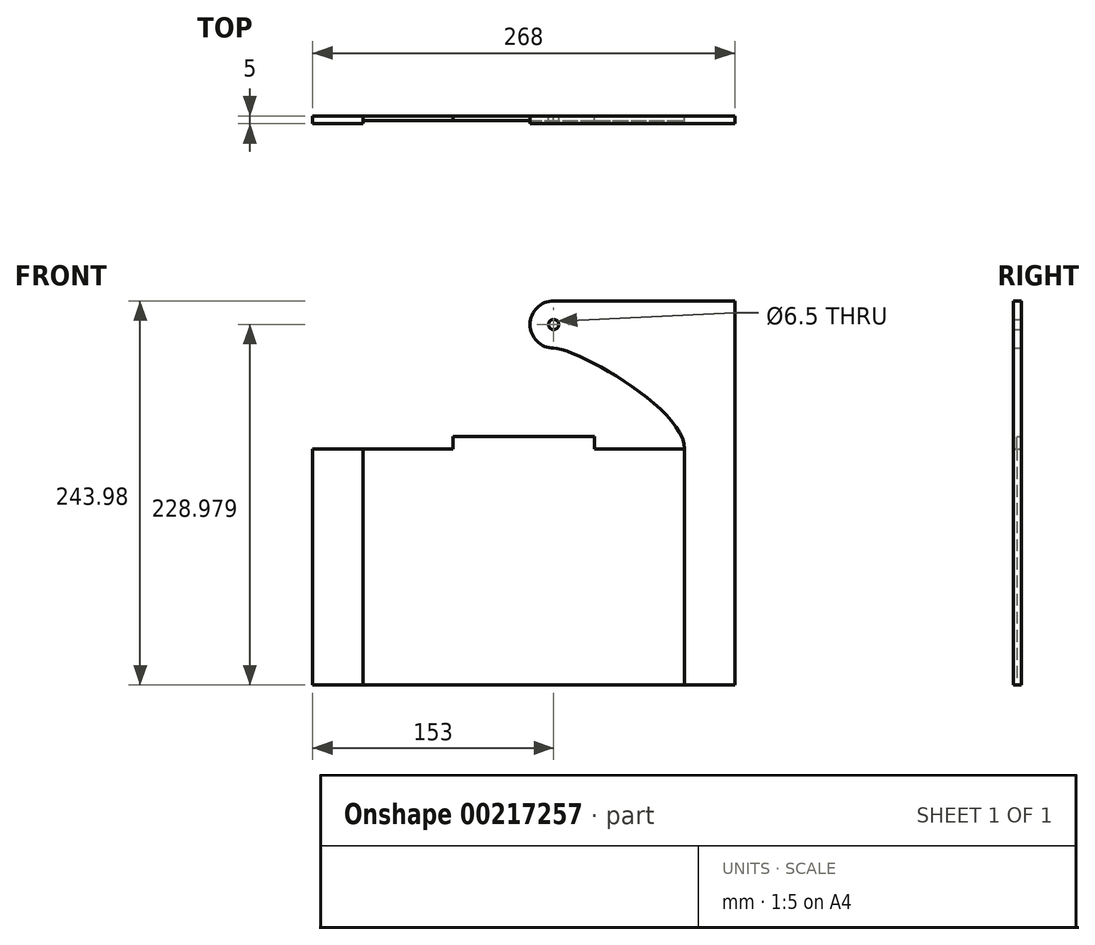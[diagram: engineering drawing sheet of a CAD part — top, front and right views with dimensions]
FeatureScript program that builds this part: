
annotation { "Feature Type Name" : "Feature", "Feature Type Description" : "" }
export const myFeature = defineFeature(function(context is Context, id is Id, definition is map)
    precondition{}
    {
        {
            var Q0;
            Q0=qCreatedBy(makeId("Front.planeOp"),FACE);
            var sketch = newSketch(context, id + "F0", { "sketchPlane" : qUnion([Q0])});
            skLineSegment(sketch, "E0.bottom", {"start": v(-134, 75) * mm, "end": v(134, 75) * mm});
            skLineSegment(sketch, "E0.top", {"start": v(-134, -75) * mm, "end": v(134, -75) * mm});
            skLineSegment(sketch, "E0.left", {"start": v(-134, 75) * mm, "end": v(-134, -75) * mm});
            skLineSegment(sketch, "E0.right", {"start": v(134, 75) * mm, "end": v(134, -75) * mm});
            skPoint(sketch, "E0.middle", {"position": v(0, 0) * mm});
            skPoint(sketch, "E1", {"position": v(-102, 75) * mm});
            skPoint(sketch, "E2", {"position": v(102, 75) * mm});
            skLineSegment(sketch, "E3", {"start": v(-102, 75) * mm, "end": v(-102, -75) * mm});
            skLineSegment(sketch, "E4", {"start": v(102, 75) * mm, "end": v(102, -75) * mm});
            skLineSegment(sketch, "E5.bottom", {"start": v(-134, 75) * mm, "end": v(-104, 75) * mm});
            skLineSegment(sketch, "E6.MirrorCS", {"start": v(102, 75) * mm, "end": v(104, 168.98) * mm});
            skLineSegment(sketch, "E7", {"start": v(134, 75) * mm, "end": v(134, 168.98) * mm});
            skLineSegment(sketch, "E8", {"start": v(134, 168.98) * mm, "end": v(104, 168.98) * mm});
            skPoint(sketch, "E9", {"position": v(0, 75) * mm});
            skLineSegment(sketch, "E10", {"start": v(0, 75) * mm, "end": v(45, 75) * mm});
            skLineSegment(sketch, "E11", {"start": v(0, 75) * mm, "end": v(-45, 75) * mm});
            skLineSegment(sketch, "E12.bottom", {"start": v(-45, 75) * mm, "end": v(45, 75) * mm});
            skLineSegment(sketch, "E12.top", {"start": v(-45, 83) * mm, "end": v(45, 83) * mm});
            skLineSegment(sketch, "E12.left", {"start": v(-45, 75) * mm, "end": v(-45, 83) * mm});
            skLineSegment(sketch, "E12.right", {"start": v(45, 75) * mm, "end": v(45, 83) * mm});
            skLineSegment(sketch, "E13", {"start": v(104, 168.98) * mm, "end": v(19, 168.98) * mm});
            skLineSegment(sketch, "E14", {"start": v(19, 168.98) * mm, "end": v(19, 138.98) * mm});
            skArc(sketch, "E15", {"start": v(19, 168.98) * mm, "mid": v(4, 153.98) * mm, "end": v(19, 138.98) * mm});
            skFitSpline(sketch, "E16", {"points": [v(19, 138.98) * mm, v(102, 75) * mm], "startDerivative": vector(45, -0.76) * mm, "endDerivative": vector(-1.6, -74.98) * mm});
            skLineSegment(sketch, "E17", {"start": v(0, 0) * mm, "end": v(0, -16.46) * mm});
            skArc(sketch, "E18.MirrorCS", {"start": v(-19, 168.98) * mm, "mid": v(-4, 153.98) * mm, "end": v(-19, 138.98) * mm});
            skFitSpline(sketch, "E19.MirrorCS", {"points": [v(-19, 138.98) * mm, v(-102, 75) * mm], "startDerivative": vector(-45, -0.76) * mm, "endDerivative": vector(1.6, -74.98) * mm});
            skLineSegment(sketch, "E20.MirrorCS", {"start": v(-104, 168.98) * mm, "end": v(-19, 168.98) * mm});
            skLineSegment(sketch, "E21.MirrorCS", {"start": v(-134, 168.98) * mm, "end": v(-104, 168.98) * mm});
            skLineSegment(sketch, "E22.MirrorCS", {"start": v(-134, 75) * mm, "end": v(-134, 168.98) * mm});
            skCircle(sketch, "E23", {"center": v(-19, 153.98) * mm, "radius": 3.25 * mm});
            skCircle(sketch, "E24.MirrorC", {"center": v(19, 153.98) * mm, "radius": 3.25 * mm});
            skSolve(sketch);
        }
        {
            var Q0;
            {var subQ0=sQuery(id+"F0.wireOp",EDGE,"E12.top");Q0=makeQuery(id+"F0.imprint","IMPRINT",FACE,{"disambiguationData":[TD([[makeQuery(id+"F0.imprint","IMPRINT",EDGE,{"derivedFrom":subQ0}),-1.0]])]});}
            var Q1;
            {var subQ0=sQuery(id+"F0.wireOp",EDGE,"E3");Q1=makeQuery(id+"F0.imprint","IMPRINT",FACE,{"disambiguationData":[TD([[makeQuery(id+"F0.imprint","IMPRINT",EDGE,{"derivedFrom":subQ0}),1.0]])]});}
            var Q2;
            {var subQ0=sQuery(id+"F0.wireOp",EDGE,"E12.bottom");Q2=makeQuery(id+"F0.imprint","IMPRINT",FACE,{"disambiguationData":[TD([[makeQuery(id+"F0.imprint","IMPRINT",EDGE,{"derivedFrom":subQ0}),1.0]])]});}
            extrude(context, id + "F1", {"entities" : qUnion([Q0, Q1, Q2]), "depth" : 3 * mm});
        }
        {
            var Q0;
            {var subQ0=sQuery(id+"F0.wireOp",EDGE,"E0.left");Q0=makeQuery(id+"F0.imprint","IMPRINT",FACE,{"disambiguationData":[TD([[makeQuery(id+"F0.imprint","IMPRINT",EDGE,{"derivedFrom":subQ0}),1.0]])]});}
            var Q1;
            {var subQ0=sQuery(id+"F0.wireOp",EDGE,"LCp1J8qT-NVfm-OEKm-3UG8-YQ4WZCoqZhsf");Q1=makeQuery(id+"F0.imprint","IMPRINT",FACE,{"disambiguationData":[TD([[makeQuery(id+"F0.imprint","IMPRINT",EDGE,{"derivedFrom":subQ0}),1.0]])]});}
            var Q2;
            {var subQ0=sQuery(id+"F0.wireOp",EDGE,"E0.right");Q2=makeQuery(id+"F0.imprint","IMPRINT",FACE,{"disambiguationData":[TD([[makeQuery(id+"F0.imprint","IMPRINT",EDGE,{"derivedFrom":subQ0}),-1.0]])]});}
            var Q3;
            Q3=makeQuery(id+"F0.imprint","IMPRINT",FACE,{"disambiguationData":[TD([[makeQuery(id+"F0.imprint","IMPRINT",EDGE,{"derivedFrom":sQuery(id+"F0.wireOp",EDGE,"E5.bottom")}),1.0]])]});
            var Q4;
            {var subQ2=sQuery(id+"F0.wireOp",EDGE,"E6.MirrorCS");Q4=makeQuery(id+"F0.imprint","IMPRINT",FACE,{"disambiguationData":[TD([[makeQuery(id+"F0.imprint","IMPRINT",EDGE,{"derivedFrom":subQ2}),-1.0]])]});}
            var Q5;
            Q5=makeQuery(id+"F0.imprint","IMPRINT",FACE,{"disambiguationData":[TD([[makeQuery(id+"F0.imprint","IMPRINT",EDGE,{"derivedFrom":sQuery(id+"F0.wireOp",EDGE,"E6.MirrorCS")}),1.0]])]});
            var Q6;
            {var subQ0=sQuery(id+"F0.wireOp",EDGE,"E15");Q6=makeQuery(id+"F0.imprint","IMPRINT",FACE,{"disambiguationData":[TD([[makeQuery(id+"F0.imprint","IMPRINT",EDGE,{"derivedFrom":subQ0}),1.0]])]});}
            extrude(context, id + "F2", {"entities" : qUnion([Q0, Q1, Q2, Q3, Q4, Q5, Q6]), "depth" : 5 * mm});
        }
    });
